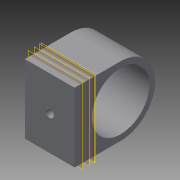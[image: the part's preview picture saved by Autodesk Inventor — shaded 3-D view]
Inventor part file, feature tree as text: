
AUTODESK INVENTOR PART (.ipt)
format: ipt  version: 2014 (Build 180170000, 170)  size: 130,560 bytes
history: native  units: mm
features: plane x4, sketch x4, extrude x2, fillet x2, hole x2
ambient origin geometry x8: Origin, YZ Plane, XZ Plane, XY Plane, X Axis, Y Axis, Z Axis, Center Point
bodies: Volumenkörper1 (feature_tree)
feature tree (14):
  extrude  "Extrusion1"  Depth=36.0mm
  fillet  "Rundung1"  Radius=26.0mm
  hole  "Bohrung1"  [1 undecoded]
  plane  "Arbeitsebene2"
  plane  "Arbeitsebene3"
  extrude  "Extrusion2"  [1 undecoded]
  fillet  "Rundung2"  [1 undecoded]
  plane  "Arbeitsebene7"
  hole  "Bohrung5"  [1 undecoded]
  sketch  "Skizze1"  dims[d0=42.0mm d1=36.0mm d2=26.0mm d3=0.0mm]
  sketch  "Skizze2"  dims[d4=18.0mm d5=30.0mm]
  sketch  "Skizze3"  dims[d6=30.0mm d7=6.0mm d8=4.0mm d9=2.0mm d10=90.0deg d11=8.0mm d12=20.594885mm d13=-3.0mm d14=-6.2mm]
  plane  "Arbeitsebene6"
  sketch  "Skizze9"  dims[d15=20.0mm d16=25.0mm d17=0.0mm d18=0.0mm d19=9.0mm d48=-0.8mm d49=13.0mm d50=18.0mm d51=4.2mm d52=6.0mm d53=10.0mm d54=2.0mm d55=90.0deg d56=15.0mm d57=0.0mm]
note: 4 required parameter values undecoded (feature->parameter linkage not recoverable at this tier; creation-order binding heuristic only, values carry confidence <= 0.55)
